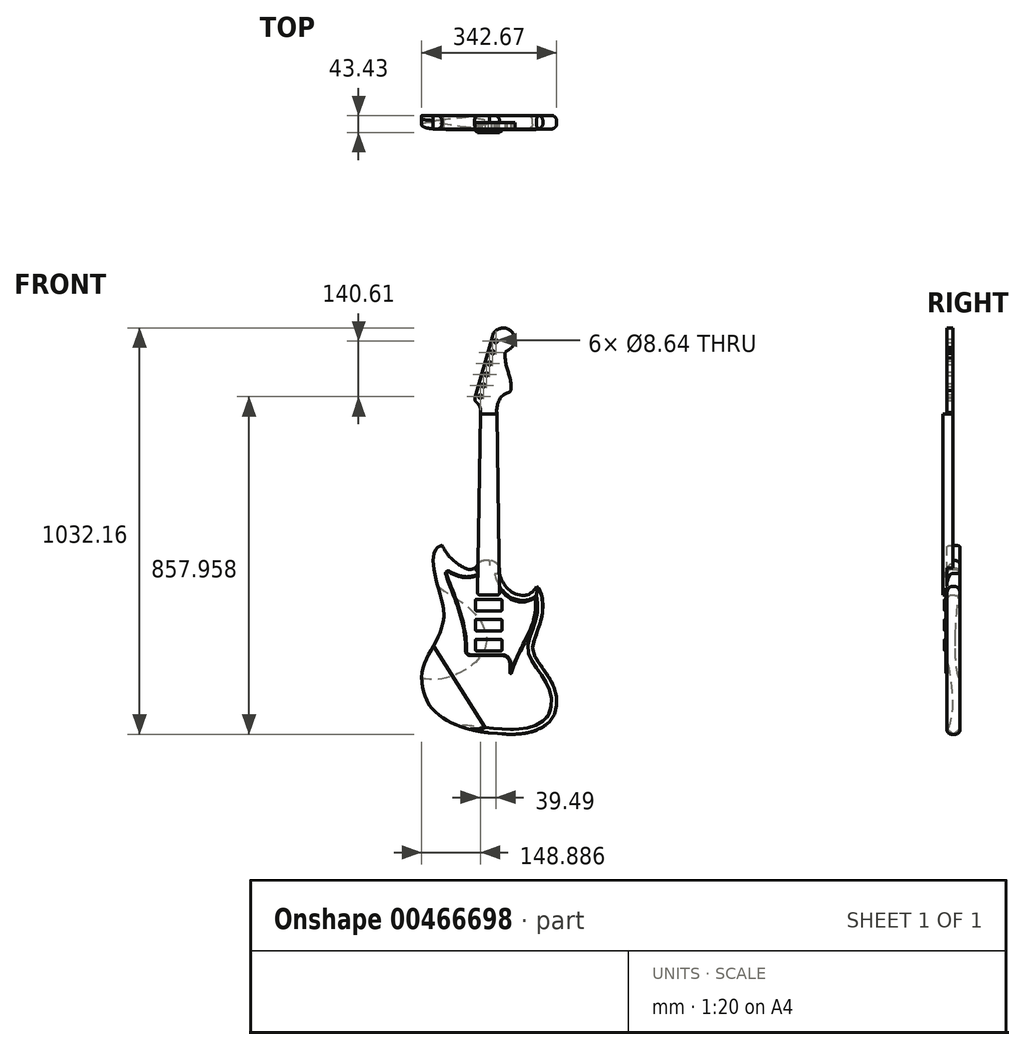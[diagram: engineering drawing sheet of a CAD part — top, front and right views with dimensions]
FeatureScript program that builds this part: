
annotation { "Feature Type Name" : "Feature", "Feature Type Description" : "" }
export const myFeature = defineFeature(function(context is Context, id is Id, definition is map)
    precondition{}
    {
        {
            var Q0;
            Q0=qCreatedBy(makeId("Front.planeOp"),FACE);
            var sketch = newSketch(context, id + "F0", { "sketchPlane" : qUnion([Q0])});
            skPoint(sketch, "E0", {"position": v(266.02, -333.89) * mm});
            skPoint(sketch, "E1", {"position": v(-78.2, -278.93) * mm});
            skPoint(sketch, "E2", {"position": v(-76.64, -280.74) * mm});
            skLineSegment(sketch, "E3", {"start": v(93.45, -416.82) * mm, "end": v(93.45, 154.69) * mm});
            skFitSpline(sketch, "E4", {"points": [v(215.27, -45.07) * mm, v(221.74, -52.76) * mm, v(227.37, -65.34) * mm, v(230.94, -92.4) * mm, v(229.66, -113.64) * mm, v(222.38, -144) * mm, v(207.76, -185.79) * mm, v(205.78, -193.7) * mm, v(205.08, -202.3) * mm, v(212.22, -224.83) * mm, v(254.9, -291.04) * mm, v(266.02, -335.63) * mm, v(264.26, -354.59) * mm, v(260.65, -368.75) * mm, v(250.4, -387.43) * mm, v(215.65, -410.17) * mm, v(172.98, -419.58) * mm, v(137.57, -420.38) * mm, v(93.45, -416.82) * mm], "startDerivative": vector(356.2, -351.19) * mm, "endDerivative": vector(-585.1, 56.64) * mm});
            skFitSpline(sketch, "E5", {"points": [v(121.13, -12.3) * mm, v(148.78, -56.88) * mm, v(178.2, -67.58) * mm, v(196.49, -64.46) * mm, v(215.27, -45.07) * mm], "startDerivative": vector(17.29, -126.3) * mm, "endDerivative": vector(64.81, 113.25) * mm});
            skFitSpline(sketch, "E6", {"points": [v(93.45, -416.82) * mm, v(3.9, -393.73) * mm, v(-39.72, -365.76) * mm, v(-64.89, -332.1) * mm, v(-76.64, -276.03) * mm, v(-67.62, -235.7) * mm, v(-46.7, -196.3) * mm, v(-31.36, -164.8) * mm, v(-22.38, -135.72) * mm, v(-20.36, -121.45) * mm, v(-21.2, -101.5) * mm, v(-32.33, -55.57) * mm, v(-41.85, -21.6) * mm, v(-47.21, 13.16) * mm, v(-45.84, 34.12) * mm, v(-39.8, 50.28) * mm, v(-29.72, 57.62) * mm, v(-25.03, 58.87) * mm], "startDerivative": vector(-990.97, 98.44) * mm, "endDerivative": vector(154.03, 27.77) * mm});
            skFitSpline(sketch, "E7", {"points": [v(-25.03, 58.87) * mm, v(5.76, 19.2) * mm, v(66.93, -2.65) * mm], "startDerivative": vector(61.81, -109.24) * mm, "endDerivative": vector(117.84, 33.66) * mm});
            skArc(sketch, "E8.filletArc", {"start": v(39.05, -0.76) * mm, "mid": v(48.72, -1.75) * mm, "end": v(57.8, 1.72) * mm});
            skLineSegment(sketch, "E9.bottom", {"start": v(95.73, 20.73) * mm, "end": v(95.73, 20.73) * mm});
            skLineSegment(sketch, "E9.top", {"start": v(67.02, -59.63) * mm, "end": v(121.13, -59.63) * mm});
            skLineSegment(sketch, "E9.left", {"start": v(67.02, 11.98) * mm, "end": v(67.02, -59.63) * mm});
            skLineSegment(sketch, "E9.right", {"start": v(121.13, -4.67) * mm, "end": v(121.13, -59.63) * mm});
            skLineSegment(sketch, "E10", {"start": v(93.45, -416.82) * mm, "end": v(-46.7, -196.3) * mm});
            skLineSegment(sketch, "E11.bottom", {"start": v(57.58, -125.48) * mm, "end": v(129.33, -125.48) * mm});
            skLineSegment(sketch, "E11.top", {"start": v(57.58, -161.04) * mm, "end": v(129.33, -161.04) * mm});
            skLineSegment(sketch, "E11.left", {"start": v(49.96, -133.1) * mm, "end": v(49.96, -153.42) * mm});
            skLineSegment(sketch, "E11.right", {"start": v(136.95, -133.1) * mm, "end": v(136.95, -153.42) * mm});
            skArc(sketch, "E12.filletArc", {"start": v(57.58, -125.48) * mm, "mid": v(52.19, -127.7) * mm, "end": v(49.96, -133.1) * mm});
            skArc(sketch, "E13.filletArc", {"start": v(136.95, -133.1) * mm, "mid": v(134.72, -127.7) * mm, "end": v(129.33, -125.48) * mm});
            skArc(sketch, "E14.filletArc", {"start": v(129.33, -161.04) * mm, "mid": v(134.72, -158.8) * mm, "end": v(136.95, -153.42) * mm});
            skArc(sketch, "E15.filletArc", {"start": v(49.96, -153.42) * mm, "mid": v(52.19, -158.8) * mm, "end": v(57.58, -161.04) * mm});
            skLineSegment(sketch, "E16", {"start": v(93.45, -125.48) * mm, "end": v(93.45, -161.04) * mm, "construction": true});
            skLineSegment(sketch, "E17", {"start": v(49.96, -143.26) * mm, "end": v(136.95, -143.26) * mm, "construction": true});
            skLineSegment(sketch, "E18.bottom", {"start": v(57.58, -74.68) * mm, "end": v(129.33, -74.68) * mm});
            skLineSegment(sketch, "E18.top", {"start": v(57.58, -110.24) * mm, "end": v(129.33, -110.24) * mm});
            skLineSegment(sketch, "E18.left", {"start": v(49.96, -82.3) * mm, "end": v(49.96, -102.62) * mm});
            skLineSegment(sketch, "E18.right", {"start": v(136.95, -82.3) * mm, "end": v(136.95, -102.62) * mm});
            skArc(sketch, "E19.filletArc", {"start": v(57.58, -74.68) * mm, "mid": v(52.19, -76.9) * mm, "end": v(49.96, -82.3) * mm});
            skArc(sketch, "E20.filletArc", {"start": v(136.95, -82.3) * mm, "mid": v(134.72, -76.9) * mm, "end": v(129.33, -74.68) * mm});
            skArc(sketch, "E21.filletArc", {"start": v(129.33, -110.24) * mm, "mid": v(134.72, -108) * mm, "end": v(136.95, -102.62) * mm});
            skArc(sketch, "E22.filletArc", {"start": v(49.96, -102.62) * mm, "mid": v(52.19, -108) * mm, "end": v(57.58, -110.24) * mm});
            skLineSegment(sketch, "E23", {"start": v(93.45, -74.68) * mm, "end": v(93.45, -110.24) * mm, "construction": true});
            skLineSegment(sketch, "E24", {"start": v(49.96, -92.46) * mm, "end": v(136.95, -92.46) * mm, "construction": true});
            skLineSegment(sketch, "E25.bottom", {"start": v(57.58, -176.28) * mm, "end": v(129.33, -176.28) * mm});
            skLineSegment(sketch, "E25.top", {"start": v(57.58, -211.84) * mm, "end": v(129.33, -211.84) * mm});
            skLineSegment(sketch, "E25.left", {"start": v(49.96, -183.9) * mm, "end": v(49.96, -204.22) * mm});
            skLineSegment(sketch, "E25.right", {"start": v(136.95, -183.9) * mm, "end": v(136.95, -204.22) * mm});
            skArc(sketch, "E26.filletArc", {"start": v(57.58, -176.28) * mm, "mid": v(52.19, -178.5) * mm, "end": v(49.96, -183.9) * mm});
            skArc(sketch, "E27.filletArc", {"start": v(136.95, -183.9) * mm, "mid": v(134.72, -178.5) * mm, "end": v(129.33, -176.28) * mm});
            skArc(sketch, "E28.filletArc", {"start": v(129.33, -211.84) * mm, "mid": v(134.72, -209.6) * mm, "end": v(136.95, -204.22) * mm});
            skArc(sketch, "E29.filletArc", {"start": v(49.96, -204.22) * mm, "mid": v(52.19, -209.6) * mm, "end": v(57.58, -211.84) * mm});
            skLineSegment(sketch, "E30", {"start": v(93.45, -176.28) * mm, "end": v(93.45, -211.84) * mm, "construction": true});
            skLineSegment(sketch, "E31", {"start": v(49.96, -194.06) * mm, "end": v(136.95, -194.06) * mm, "construction": true});
            skPoint(sketch, "E32.visualSharp", {"position": v(121.13, 20.73) * mm});
            skArc(sketch, "E32.filletArc", {"start": v(121.13, -4.67) * mm, "mid": v(113.7, 13.3) * mm, "end": v(95.73, 20.73) * mm});
            skFitSpline(sketch, "E33", {"points": [v(95.73, 20.73) * mm, v(73.37, 17.96) * mm, v(57.8, 1.72) * mm], "startDerivative": vector(-43.43, -1.27) * mm, "endDerivative": vector(-37.77, -27.72) * mm});
            skSolve(sketch);
        }
        {
            var Q0;
            {var subQ0=sQuery(id+"F0.wireOp",EDGE,"E10");Q0=makeQuery(id+"F0.imprint","IMPRINT",FACE,{"disambiguationData":[TD([[makeQuery(id+"F0.imprint","IMPRINT",EDGE,{"derivedFrom":subQ0}),1.0]])]});}
            extrude(context, id + "F1", {"entities" : qUnion([Q0]), "depth" : 33.9 * mm});
        }
        {
            var Q0;
            Q0=makeQuery(id+"F1.opExtrude","SWEPT_EDGE",EDGE,{"disambiguationData":[OSD([sQuery(id+"F0.wireOp",EDGE,"E3"),sQuery(id+"F0.wireOp",EDGE,"E4"),sQuery(id+"F0.wireOp",EDGE,"E6"),sQuery(id+"F0.wireOp",EDGE,"E10")])]});
            var Q1;
            Q1=sQuery(id+"F0.wireOp",EDGE,"E10");
            cPlane(context, id + "F2", {"entities" : qUnion([Q0, Q1]), "cplaneType" : CPlaneType.LINE_ANGLE, "offset" : 25.4 * mm, "angle" : 90 * degree, "width" : 152.4 * mm, "height" : 152.4 * mm});
        }
        {
            var Q0;
            Q0=qCreatedBy(id+"F2.planeOp",FACE);
            var sketch = newSketch(context, id + "F3", { "sketchPlane" : qUnion([Q0])});
            skFitSpline(sketch, "E34", {"points": [v(-144.71, 33.92) * mm, v(-234.18, 18.01) * mm], "startDerivative": vector(-88.6, -4.87) * mm, "endDerivative": vector(-122.95, -37.49) * mm});
            skLineSegment(sketch, "E35", {"start": v(-234.18, 18.01) * mm, "end": v(-234.18, 35.25) * mm});
            skLineSegment(sketch, "E36", {"start": v(-234.18, 35.25) * mm, "end": v(-144.71, 35.25) * mm});
            skLineSegment(sketch, "E37", {"start": v(-144.71, 33.92) * mm, "end": v(-144.71, 35.25) * mm});
            skSolve(sketch);
        }
        {
            var Q0;
            Q0=makeQuery(id+"F3.imprint","IMPRINT",FACE,{"disambiguationData":[TD([[makeQuery(id+"F3.imprint","IMPRINT",EDGE,{"derivedFrom":sQuery(id+"F3.wireOp",EDGE,"E34")}),-1.0]])]});
            extrude(context, id + "F4", {"entities" : qUnion([Q0]), "operationType" : NewBodyOperationType.REMOVE, "endBound" : BoundingType.THROUGH_ALL, "oppositeDirection" : true, "depth" : 274.32 * mm});
        }
        {
            var Q0;
            {var subQ1=sQuery(id+"F0.wireOp",EDGE,"E7");Q0=makeQuery(id+"F0.imprint","IMPRINT",FACE,{"disambiguationData":[TD([[makeQuery(id+"F0.imprint","IMPRINT",EDGE,{"derivedFrom":subQ1}),-1.0]])]});}
            var Q1;
            {var subQ5=sQuery(id+"F0.wireOp",EDGE,"E4");Q1=makeQuery(id+"F0.imprint","IMPRINT",FACE,{"disambiguationData":[TD([[makeQuery(id+"F0.imprint","IMPRINT",EDGE,{"derivedFrom":subQ5}),-1.0]])]});}
            var Q2;
            {var subQ2=sQuery(id+"F0.wireOp",EDGE,"E9.bottom");var subQ4=sQuery(id+"F0.wireOp",EDGE,"E3");var subQ5=makeQuery(id+"F0.imprint","INTERSECT",VERTEX,{"derivedFrom":[subQ4,subQ2]});Q2=makeQuery(id+"F0.imprint","IMPRINT",FACE,{"disambiguationData":[TD([[makeQuery(id+"F0.imprint","IMPRINT",EDGE,{"disambiguationData":[TD([[subQ5,1.0]])],"derivedFrom":subQ4}),-1.0]])]});}
            var Q3;
            {var subQ2=sQuery(id+"F0.wireOp",EDGE,"E9.bottom");var subQ4=sQuery(id+"F0.wireOp",EDGE,"E3");var subQ5=makeQuery(id+"F0.imprint","INTERSECT",VERTEX,{"derivedFrom":[subQ4,subQ2]});Q3=makeQuery(id+"F0.imprint","IMPRINT",FACE,{"disambiguationData":[TD([[makeQuery(id+"F0.imprint","IMPRINT",EDGE,{"disambiguationData":[TD([[subQ5,1.0]])],"derivedFrom":subQ4}),1.0]])]});}
            var Q4;
            Q4=makeQuery(id+"F0.imprint","IMPRINT",FACE,{"disambiguationData":[TD([[makeQuery(id+"F0.imprint","IMPRINT",EDGE,{"derivedFrom":sQuery(id+"F0.wireOp",EDGE,"E18.right")}),-1.0]])]});
            var Q5;
            Q5=makeQuery(id+"F0.imprint","IMPRINT",FACE,{"disambiguationData":[TD([[makeQuery(id+"F0.imprint","IMPRINT",EDGE,{"derivedFrom":sQuery(id+"F0.wireOp",EDGE,"E18.left")}),1.0]])]});
            var Q6;
            Q6=makeQuery(id+"F0.imprint","IMPRINT",FACE,{"disambiguationData":[TD([[makeQuery(id+"F0.imprint","IMPRINT",EDGE,{"derivedFrom":sQuery(id+"F0.wireOp",EDGE,"E11.left")}),1.0]])]});
            var Q7;
            Q7=makeQuery(id+"F0.imprint","IMPRINT",FACE,{"disambiguationData":[TD([[makeQuery(id+"F0.imprint","IMPRINT",EDGE,{"derivedFrom":sQuery(id+"F0.wireOp",EDGE,"E11.right")}),-1.0]])]});
            var Q8;
            Q8=makeQuery(id+"F0.imprint","IMPRINT",FACE,{"disambiguationData":[TD([[makeQuery(id+"F0.imprint","IMPRINT",EDGE,{"derivedFrom":sQuery(id+"F0.wireOp",EDGE,"E25.right")}),-1.0]])]});
            var Q9;
            Q9=makeQuery(id+"F0.imprint","IMPRINT",FACE,{"disambiguationData":[TD([[makeQuery(id+"F0.imprint","IMPRINT",EDGE,{"derivedFrom":sQuery(id+"F0.wireOp",EDGE,"E25.left")}),1.0]])]});
            var Q10;
            {var subQ8=sQuery(id+"F0.wireOp",EDGE,"E32.filletArc");Q10=makeQuery(id+"F0.imprint","IMPRINT",FACE,{"disambiguationData":[TD([[makeQuery(id+"F0.imprint","IMPRINT",EDGE,{"derivedFrom":subQ8}),1.0]])]});}
            var Q11;
            {var subQ5=sQuery(id+"F0.wireOp",EDGE,"E9.left");Q11=makeQuery(id+"F0.imprint","IMPRINT",FACE,{"disambiguationData":[TD([[makeQuery(id+"F0.imprint","IMPRINT",EDGE,{"derivedFrom":subQ5}),1.0]])]});}
            extrude(context, id + "F5", {"entities" : qUnion([Q0, Q1, Q2, Q3, Q4, Q5, Q6, Q7, Q8, Q9, Q10, Q11]), "operationType" : NewBodyOperationType.ADD, "depth" : 33.9 * mm});
        }
        {
            var Q0;
            {var subQ1=sQuery(id+"F0.wireOp",EDGE,"E7");Q0=makeQuery(id+"F0.imprint","IMPRINT",FACE,{"disambiguationData":[TD([[makeQuery(id+"F0.imprint","IMPRINT",EDGE,{"derivedFrom":subQ1}),-1.0]])]});}
            var sketch = newSketch(context, id + "F6", { "sketchPlane" : qUnion([Q0])});
            skFitSpline(sketch, "E38", {"points": [v(-56.72, -25.02) * mm, v(27.3, -87.2) * mm, v(83.7, -155.44) * mm, v(73.57, -221.77) * mm, v(-76.43, -278.56) * mm], "startDerivative": vector(46.73, -161.4) * mm, "endDerivative": vector(-591.69, 127.24) * mm});
            skLineSegment(sketch, "E39", {"start": v(-56.72, -25.02) * mm, "end": v(-76.43, -278.56) * mm});
            skLineSegment(sketch, "E40", {"start": v(87.74, -184.34) * mm, "end": v(-206.93, -143.72) * mm});
            skSolve(sketch);
        }
        {
            var Q0;
            Q0=sQuery(id+"F6.wireOp",EDGE,"E40");
            cPlane(context, id + "F7", {"entities" : qUnion([Q0]), "cplaneType" : CPlaneType.LINE_ANGLE, "offset" : 25.4 * mm, "angle" : 90 * degree, "width" : 152.4 * mm, "height" : 152.4 * mm});
        }
        {
            var Q0;
            Q0=qCreatedBy(id+"F7.planeOp",FACE);
            var sketch = newSketch(context, id + "F8", { "sketchPlane" : qUnion([Q0])});
            skLineSegment(sketch, "E41", {"start": v(112.3, 0) * mm, "end": v(-53.56, -16.1) * mm});
            skSolve(sketch);
        }
        {
            var Q0;
            {var subQ0=sQuery(id+"F6.wireOp",EDGE,"E40");var subQ1=sQuery(id+"F6.wireOp",EDGE,"E38");var subQ2=makeQuery(id+"F6.imprint","INTERSECT",VERTEX,{"derivedFrom":[subQ1,subQ0]});Q0=makeQuery(id+"F6.imprint","IMPRINT",FACE,{"disambiguationData":[TD([[makeQuery(id+"F6.imprint","IMPRINT",EDGE,{"disambiguationData":[TD([[subQ2,1.0]])],"derivedFrom":subQ1}),-1.0]])]});}
            var Q1;
            {var subQ0=sQuery(id+"F6.wireOp",EDGE,"E40");var subQ1=sQuery(id+"F6.wireOp",EDGE,"E38");var subQ2=makeQuery(id+"F6.imprint","INTERSECT",VERTEX,{"derivedFrom":[subQ1,subQ0]});Q1=makeQuery(id+"F6.imprint","IMPRINT",FACE,{"disambiguationData":[TD([[makeQuery(id+"F6.imprint","IMPRINT",EDGE,{"disambiguationData":[TD([[subQ2,-1.0]])],"derivedFrom":subQ1}),-1.0]])]});}
            var Q2;
            {var subQ7=sQuery(id+"F6.wireOp",EDGE,"E39");var subQ8=sQuery(id+"F6.wireOp",EDGE,"E38");var subQ9=makeQuery(id+"F6.imprint","INTERSECT",VERTEX,{"disambiguationData":[OD(1.0)],"derivedFrom":[subQ8,subQ7]});Q2=makeQuery(id+"F6.imprint","IMPRINT",FACE,{"disambiguationData":[TD([[makeQuery(id+"F6.imprint","IMPRINT",EDGE,{"disambiguationData":[TD([[subQ9,1.0]])],"derivedFrom":subQ8}),-1.0]])]});}
            var Q3;
            {var subQ0=sQuery(id+"F6.wireOp",EDGE,"E39");var subQ1=sQuery(id+"F6.wireOp",EDGE,"E38");var subQ2=makeQuery(id+"F6.imprint","INTERSECT",VERTEX,{"disambiguationData":[OD(0.0)],"derivedFrom":[subQ1,subQ0]});Q3=makeQuery(id+"F6.imprint","IMPRINT",FACE,{"disambiguationData":[TD([[makeQuery(id+"F6.imprint","IMPRINT",EDGE,{"disambiguationData":[TD([[subQ2,-1.0]])],"derivedFrom":subQ0}),1.0]])]});}
            var Q4;
            {var subQ9=sQuery(id+"F0.wireOp",EDGE,"E29.filletArc");var subQ10=makeQuery(id+"F0.imprint","IMPRINT",EDGE,{"derivedFrom":subQ9});Q4=makeQuery(id+"F6.imprint","IMPRINT",FACE,{"disambiguationData":[TD([[makeQuery(id+"F6.imprint","IMPRINT",EDGE,{"derivedFrom":subQ10}),-1.0]])]});}
            var Q5;
            Q5=makeQuery(id+"F6.imprint","IMPRINT",FACE,{"disambiguationData":[TD([[makeQuery(id+"F6.imprint","IMPRINT",EDGE,{"derivedFrom":makeQuery(id+"F0.imprint","IMPRINT",EDGE,{"derivedFrom":sQuery(id+"F0.wireOp",EDGE,"E11.left")})}),-1.0]])]});
            var Q6;
            Q6=makeQuery(id+"F6.imprint","IMPRINT",FACE,{"disambiguationData":[TD([[makeQuery(id+"F6.imprint","IMPRINT",EDGE,{"derivedFrom":makeQuery(id+"F0.imprint","IMPRINT",EDGE,{"derivedFrom":sQuery(id+"F0.wireOp",EDGE,"E11.left")})}),1.0]])]});
            var Q7;
            Q7=sQuery(id+"F8.wireOp",EDGE,"E41");
            sweep(context, id + "F9", {"operationType" : NewBodyOperationType.REMOVE, "profiles" : qUnion([Q0, Q1, Q2, Q3, Q4, Q5, Q6]), "path" : qUnion([Q7])});
        }
        {
            var Q0;
            {var subQ0=sQuery(id+"F0.wireOp",EDGE,"E10");var subQ1=sQuery(id+"F0.wireOp",EDGE,"E6");Q0=makeQuery(id+"F5.boolean.opBoolean","MERGE",FACE,{"derivedFrom":[makeQuery(id+"F1.opExtrude","CAP_FACE",FACE,{"disambiguationData":[OSD([subQ1,subQ0])],"isStart":false}),makeQuery(id+"F5.opExtrude","CAP_FACE",FACE,{"disambiguationData":[OSD([sQuery(id+"F0.wireOp",EDGE,"E4"),sQuery(id+"F0.wireOp",EDGE,"E5"),subQ1,sQuery(id+"F0.wireOp",EDGE,"E7"),sQuery(id+"F0.wireOp",EDGE,"E8.filletArc"),sQuery(id+"F0.wireOp",EDGE,"E9.bottom"),sQuery(id+"F0.wireOp",EDGE,"E9.right"),subQ0,sQuery(id+"F0.wireOp",EDGE,"E11.bottom"),sQuery(id+"F0.wireOp",EDGE,"E11.top"),sQuery(id+"F0.wireOp",EDGE,"E11.left"),sQuery(id+"F0.wireOp",EDGE,"E11.right"),sQuery(id+"F0.wireOp",EDGE,"E12.filletArc"),sQuery(id+"F0.wireOp",EDGE,"E13.filletArc"),sQuery(id+"F0.wireOp",EDGE,"E14.filletArc"),sQuery(id+"F0.wireOp",EDGE,"E15.filletArc"),sQuery(id+"F0.wireOp",EDGE,"E18.bottom"),sQuery(id+"F0.wireOp",EDGE,"E18.top"),sQuery(id+"F0.wireOp",EDGE,"E18.left"),sQuery(id+"F0.wireOp",EDGE,"E18.right"),sQuery(id+"F0.wireOp",EDGE,"E19.filletArc"),sQuery(id+"F0.wireOp",EDGE,"E20.filletArc"),sQuery(id+"F0.wireOp",EDGE,"E21.filletArc"),sQuery(id+"F0.wireOp",EDGE,"E22.filletArc"),sQuery(id+"F0.wireOp",EDGE,"E25.bottom"),sQuery(id+"F0.wireOp",EDGE,"E25.top"),sQuery(id+"F0.wireOp",EDGE,"E25.left"),sQuery(id+"F0.wireOp",EDGE,"E25.right"),sQuery(id+"F0.wireOp",EDGE,"E26.filletArc"),sQuery(id+"F0.wireOp",EDGE,"E27.filletArc"),sQuery(id+"F0.wireOp",EDGE,"E28.filletArc"),sQuery(id+"F0.wireOp",EDGE,"E29.filletArc"),sQuery(id+"F0.wireOp",EDGE,"E32.filletArc"),sQuery(id+"F0.wireOp",EDGE,"5da029f0-0d08-4df7-a96a-8b1ca544c31f.filletArc")])],"isStart":false})]});}
            var sketch = newSketch(context, id + "F10", { "sketchPlane" : qUnion([Q0])});
            skLineSegment(sketch, "E42", {"start": v(114.09, 393.44) * mm, "end": v(72.81, 393.44) * mm});
            skArc(sketch, "E43", {"start": v(152.05, 562.26) * mm, "mid": v(145.08, 607.74) * mm, "end": v(102.61, 590.03) * mm});
            skLineSegment(sketch, "E44", {"start": v(114.09, 396.48) * mm, "end": v(72.81, 396.48) * mm});
            skArc(sketch, "E45", {"start": v(139.6, 553.2) * mm, "mid": v(136.44, 550.5) * mm, "end": v(134.97, 546.6) * mm});
            skFitSpline(sketch, "E46", {"points": [v(134.97, 546.6) * mm, v(134.92, 539.54) * mm, v(135.3, 534.72) * mm], "startDerivative": vector(-2.42, -13.24) * mm, "endDerivative": vector(1.68, -15.84) * mm});
            skFitSpline(sketch, "E47", {"points": [v(135.3, 534.72) * mm, v(136.98, 522.82) * mm, v(141.32, 505.32) * mm, v(145.61, 491.19) * mm, v(149.98, 471.63) * mm, v(150.16, 455.36) * mm, v(149.34, 452.34) * mm], "startDerivative": vector(10.58, -89.44) * mm, "endDerivative": vector(-11.19, -29.44) * mm});
            skFitSpline(sketch, "E48", {"points": [v(152.05, 562.26) * mm, v(147, 557.6) * mm, v(141.78, 554.47) * mm, v(139.6, 553.2) * mm], "startDerivative": vector(-11.63, -12.96) * mm, "endDerivative": vector(-8.03, -4.83) * mm});
            skLineSegment(sketch, "E49", {"start": v(102.61, 590.03) * mm, "end": v(59.05, 434.9) * mm});
            skFitSpline(sketch, "E50", {"points": [v(114.09, 396.48) * mm, v(114.26, 407.46) * mm, v(116.53, 419.52) * mm, v(118.87, 425.81) * mm, v(123.45, 433.9) * mm, v(131.73, 441.98) * mm, v(139.43, 446.23) * mm, v(146.53, 449.2) * mm, v(148.1, 450.53) * mm, v(149.34, 452.34) * mm], "startDerivative": vector(-2.24, 78.28) * mm, "endDerivative": vector(20.59, 31.93) * mm});
            skFitSpline(sketch, "E51", {"points": [v(72.81, 396.48) * mm, v(72.81, 400.36) * mm, v(72.71, 404.86) * mm, v(71.11, 411.28) * mm, v(68.48, 416.27) * mm, v(63.92, 421.76) * mm, v(60.07, 425.65) * mm], "startDerivative": vector(-0.26, 27.66) * mm, "endDerivative": vector(-26.41, 27.38) * mm});
            skFitSpline(sketch, "E52", {"points": [v(60.07, 425.65) * mm, v(59.17, 426.96) * mm, v(58.58, 428.1) * mm, v(58.35, 429.15) * mm, v(58.4, 430.68) * mm, v(58.53, 431.89) * mm, v(58.76, 433.48) * mm, v(59.05, 434.9) * mm], "startDerivative": vector(-9.65, 12.38) * mm, "endDerivative": vector(1.99, 9.31) * mm});
            skLineSegment(sketch, "E53", {"start": v(114.09, 396.48) * mm, "end": v(114.09, 393.44) * mm});
            skLineSegment(sketch, "E54", {"start": v(72.81, 396.48) * mm, "end": v(72.81, 393.44) * mm});
            skLineSegment(sketch, "E55", {"start": v(93.45, 393.44) * mm, "end": v(93.45, -76) * mm, "construction": true});
            skLineSegment(sketch, "E56", {"start": v(93.45, -56.52) * mm, "end": v(65.66, -56.52) * mm});
            skLineSegment(sketch, "E57", {"start": v(93.45, -56.52) * mm, "end": v(121.24, -56.52) * mm});
            skLineSegment(sketch, "E58", {"start": v(121.24, -56.52) * mm, "end": v(114.09, 393.44) * mm});
            skLineSegment(sketch, "E59", {"start": v(72.81, 393.44) * mm, "end": v(65.66, -56.52) * mm});
            skLineSegment(sketch, "E60", {"start": v(114.96, -67.31) * mm, "end": v(71.94, -67.31) * mm});
            skLineSegment(sketch, "E61", {"start": v(121.24, -56.52) * mm, "end": v(121.3, -60.86) * mm});
            skLineSegment(sketch, "E62", {"start": v(65.66, -56.52) * mm, "end": v(65.6, -60.86) * mm});
            skArc(sketch, "E63", {"start": v(65.6, -60.86) * mm, "mid": v(67.42, -65.42) * mm, "end": v(71.94, -67.31) * mm});
            skArc(sketch, "E64", {"start": v(114.96, -67.31) * mm, "mid": v(119.48, -65.42) * mm, "end": v(121.3, -60.86) * mm});
            skLineSegment(sketch, "E65", {"start": v(64.88, 411.04) * mm, "end": v(127, 632.25) * mm});
            skCircle(sketch, "E66", {"center": v(111.74, 577.89) * mm, "radius": 4.32 * mm});
            skCircle(sketch, "E67", {"center": v(103.84, 549.77) * mm, "radius": 4.32 * mm});
            skCircle(sketch, "E68", {"center": v(95.94, 521.64) * mm, "radius": 4.32 * mm});
            skCircle(sketch, "E69", {"center": v(88.04, 493.52) * mm, "radius": 4.32 * mm});
            skCircle(sketch, "E70", {"center": v(80.14, 465.4) * mm, "radius": 4.32 * mm});
            skCircle(sketch, "E71", {"center": v(72.25, 437.28) * mm, "radius": 4.32 * mm});
            skLineSegment(sketch, "E72", {"start": v(93.45, 370.83) * mm, "end": v(93.45, -10.17) * mm});
            skPoint(sketch, "E73", {"position": v(93.4, -232.04) * mm});
            skPoint(sketch, "E73.positionSnap0", {"position": v(93.4, -211.03) * mm});
            skSolve(sketch);
        }
        {
            var Q0;
            {var subQ9=sQuery(id+"F10.wireOp",EDGE,"E56");Q0=makeQuery(id+"F10.imprint","IMPRINT",FACE,{"disambiguationData":[TD([[makeQuery(id+"F10.imprint","IMPRINT",EDGE,{"derivedFrom":subQ9}),1.0]])]});}
            var Q1;
            {var subQ0=sQuery(id+"F10.wireOp",EDGE,"E61");Q1=makeQuery(id+"F10.imprint","IMPRINT",FACE,{"disambiguationData":[TD([[makeQuery(id+"F10.imprint","IMPRINT",EDGE,{"derivedFrom":subQ0}),-1.0]])]});}
            var Q2;
            {var subQ1=sQuery(id+"F10.wireOp",EDGE,"E42");Q2=makeQuery(id+"F10.imprint","IMPRINT",FACE,{"disambiguationData":[TD([[makeQuery(id+"F10.imprint","IMPRINT",EDGE,{"derivedFrom":subQ1}),1.0]])]});}
            var Q3;
            {var subQ1=sQuery(id+"F10.wireOp",EDGE,"E56");Q3=makeQuery(id+"F10.imprint","IMPRINT",FACE,{"disambiguationData":[TD([[makeQuery(id+"F10.imprint","IMPRINT",EDGE,{"derivedFrom":subQ1}),-1.0]])]});}
            var Q4;
            {var subQ1=sQuery(id+"F10.wireOp",EDGE,"E44");Q4=makeQuery(id+"F10.imprint","IMPRINT",FACE,{"disambiguationData":[TD([[makeQuery(id+"F10.imprint","IMPRINT",EDGE,{"derivedFrom":subQ1}),-1.0]])]});}
            var Q5;
            {var subQ9=sQuery(id+"F10.wireOp",EDGE,"E49");Q5=makeQuery(id+"F10.imprint","IMPRINT",FACE,{"disambiguationData":[TD([[makeQuery(id+"F10.imprint","IMPRINT",EDGE,{"derivedFrom":subQ9}),1.0]])]});}
            var Q6;
            Q6=makeQuery(id+"F10.imprint","IMPRINT",FACE,{"disambiguationData":[TD([[makeQuery(id+"F10.imprint","IMPRINT",EDGE,{"derivedFrom":sQuery(id+"F10.wireOp",EDGE,"E42")}),-1.0]])]});
            var Q7;
            Q7 = qSketchRegion(id + "F8", true);
            extrude(context, id + "F11", {"entities" : qUnion([Q0, Q1, Q2, Q3, Q4, Q5, Q6, Q7]), "operationType" : NewBodyOperationType.ADD, "oppositeDirection" : true, "depth" : 15.88 * mm});
        }
        {
            var Q0;
            {var subQ9=sQuery(id+"F10.wireOp",EDGE,"E56");Q0=makeQuery(id+"F10.imprint","IMPRINT",FACE,{"disambiguationData":[TD([[makeQuery(id+"F10.imprint","IMPRINT",EDGE,{"derivedFrom":subQ9}),1.0]])]});}
            var Q1;
            {var subQ0=sQuery(id+"F10.wireOp",EDGE,"E61");Q1=makeQuery(id+"F10.imprint","IMPRINT",FACE,{"disambiguationData":[TD([[makeQuery(id+"F10.imprint","IMPRINT",EDGE,{"derivedFrom":subQ0}),-1.0]])]});}
            var Q2;
            {var subQ1=sQuery(id+"F10.wireOp",EDGE,"E42");Q2=makeQuery(id+"F10.imprint","IMPRINT",FACE,{"disambiguationData":[TD([[makeQuery(id+"F10.imprint","IMPRINT",EDGE,{"derivedFrom":subQ1}),1.0]])]});}
            var Q3;
            {var subQ1=sQuery(id+"F10.wireOp",EDGE,"E56");Q3=makeQuery(id+"F10.imprint","IMPRINT",FACE,{"disambiguationData":[TD([[makeQuery(id+"F10.imprint","IMPRINT",EDGE,{"derivedFrom":subQ1}),-1.0]])]});}
            extrude(context, id + "F12", {"entities" : qUnion([Q0, Q1, Q2, Q3]), "operationType" : NewBodyOperationType.ADD, "depth" : 9.52 * mm});
        }
        {
            var Q0;
            {var subQ0=sQuery(id+"F0.wireOp",EDGE,"E6");Q0=makeQuery(id+"F5.boolean.opBoolean","MERGE",EDGE,{"derivedFrom":[makeQuery(id+"F4.boolean.opBoolean","SPLIT",EDGE,{"disambiguationData":[OD(1.0)],"derivedFrom":makeQuery(id+"F1.opExtrude","CAP_EDGE",EDGE,{"disambiguationData":[OSD([subQ0])],"isStart":false})}),makeQuery(id+"F5.opExtrude","CAP_EDGE",EDGE,{"disambiguationData":[OSD([subQ0])],"isStart":false})]});}
            var Q1;
            Q1=makeQuery(id+"F5.opExtrude","CAP_EDGE",EDGE,{"disambiguationData":[OSD([sQuery(id+"F0.wireOp",EDGE,"E4")])],"isStart":true});
            var Q2;
            Q2=makeQuery(id+"F5.opExtrude","CAP_EDGE",EDGE,{"disambiguationData":[OSD([sQuery(id+"F0.wireOp",EDGE,"E4")])],"isStart":false});
            var Q3;
            Q3=makeQuery(id+"F5.opExtrude","CAP_EDGE",EDGE,{"disambiguationData":[OSD([sQuery(id+"F0.wireOp",EDGE,"E5")])],"isStart":false});
            var Q4;
            Q4=makeQuery(id+"F5.opExtrude","CAP_EDGE",EDGE,{"disambiguationData":[OSD([sQuery(id+"F0.wireOp",EDGE,"E5")])],"isStart":true});
            var Q5;
            Q5=makeQuery(id+"F5.opExtrude","CAP_EDGE",EDGE,{"disambiguationData":[OSD([sQuery(id+"F0.wireOp",EDGE,"E7")])],"isStart":true});
            var Q6;
            Q6=makeQuery(id+"F5.opExtrude","CAP_EDGE",EDGE,{"disambiguationData":[OSD([sQuery(id+"F0.wireOp",EDGE,"E7")])],"isStart":false});
            var Q7;
            {var subQ1=sQuery(id+"F0.wireOp",EDGE,"E7");var subQ2=sQuery(id+"F0.wireOp",EDGE,"E6");Q7=makeQuery(id+"F9.boolean.opBoolean","SPLIT",EDGE,{"disambiguationData":[TD([makeQuery(id+"F5.opExtrude","SWEPT_FACE",FACE,{"disambiguationData":[OSD([subQ1])]})])],"derivedFrom":makeQuery(id+"F5.boolean.opBoolean","MERGE",EDGE,{"derivedFrom":[makeQuery(id+"F1.opExtrude","CAP_EDGE",EDGE,{"disambiguationData":[OSD([subQ2])],"isStart":true}),makeQuery(id+"F5.opExtrude","CAP_EDGE",EDGE,{"disambiguationData":[OSD([subQ2])],"isStart":true})]})});}
            var Q8;
            Q8=makeQuery(id+"F5.opExtrude","CAP_EDGE",EDGE,{"disambiguationData":[OSD([sQuery(id+"F0.wireOp",EDGE,"E8.filletArc")])],"isStart":true});
            var Q9;
            Q9=makeQuery(id+"F5.opExtrude","CAP_EDGE",EDGE,{"disambiguationData":[OSD([sQuery(id+"F0.wireOp",EDGE,"E33")])],"isStart":true});
            var Q10;
            Q10=makeQuery(id+"F5.opExtrude","CAP_EDGE",EDGE,{"disambiguationData":[OSD([sQuery(id+"F0.wireOp",EDGE,"E32.filletArc")])],"isStart":true});
            var Q11;
            Q11=makeQuery(id+"F5.opExtrude","CAP_EDGE",EDGE,{"disambiguationData":[OSD([sQuery(id+"F0.wireOp",EDGE,"E8.filletArc")])],"isStart":false});
            var Q12;
            Q12=makeQuery(id+"F5.opExtrude","CAP_EDGE",EDGE,{"disambiguationData":[OSD([sQuery(id+"F0.wireOp",EDGE,"E33")])],"isStart":false});
            fillet(context, id + "F13", {"entities" : qUnion([Q0, Q1, Q2, Q3, Q4, Q5, Q6, Q7, Q8, Q9, Q10, Q11, Q12]), "radius" : 12.7 * mm, "tangentPropagation" : true, "allowEdgeOverflow" : false});
        }
        {
            var Q0;
            Q0=makeQuery(id+"F10.imprint","IMPRINT",FACE,{"disambiguationData":[TD([[makeQuery(id+"F10.imprint","IMPRINT",EDGE,{"derivedFrom":sQuery(id+"F10.wireOp",EDGE,"E60")}),1.0]])]});
            var sketch = newSketch(context, id + "F14", { "sketchPlane" : qUnion([Q0])});
            skFitSpline(sketch, "E74.0", {"points": [v(214.49, -66.79) * mm, v(213.66, -67.6) * mm, v(211.95, -69.17) * mm, v(209.26, -71.36) * mm, v(206.42, -73.38) * mm, v(203.48, -75.17) * mm, v(200.43, -76.7) * mm, v(197.78, -77.77) * mm, v(195.6, -78.5) * mm, v(193.92, -78.96) * mm, v(192.22, -79.37) * mm, v(189.96, -79.8) * mm, v(187.1, -80.18) * mm, v(183.67, -80.4) * mm, v(180.22, -80.4) * mm, v(176.76, -80.24) * mm, v(173.3, -79.94) * mm, v(169.86, -79.49) * mm, v(166.48, -78.87) * mm, v(163.14, -78.08) * mm, v(159.86, -77.11) * mm, v(156.62, -75.96) * mm, v(153.97, -74.83) * mm, v(151.88, -73.84) * mm, v(149.82, -72.78) * mm, v(147.33, -71.36) * mm, v(144.44, -69.5) * mm, v(141.67, -67.48) * mm, v(139, -65.32) * mm, v(136.44, -63.01) * mm, v(133.97, -60.58) * mm, v(131.6, -58.07) * mm, v(128.57, -54.6) * mm, v(125.01, -50.1) * mm, v(122.39, -46.3) * mm, v(121.13, -44.37) * mm]});
            skPoint(sketch, "E75", {"position": v(195.9, -173.4) * mm});
            skLineSegment(sketch, "E76.0", {"start": v(114.96, -67.31) * mm, "end": v(71.94, -67.31) * mm});
            skLineSegment(sketch, "E77.0", {"start": v(72.81, 393.44) * mm, "end": v(65.66, -56.52) * mm});
            skArc(sketch, "E77.1", {"start": v(65.6, -60.86) * mm, "mid": v(67.42, -65.42) * mm, "end": v(71.94, -67.31) * mm});
            skLineSegment(sketch, "E77.2", {"start": v(65.66, -56.52) * mm, "end": v(65.6, -60.86) * mm});
            skArc(sketch, "E77.4", {"start": v(114.96, -67.31) * mm, "mid": v(119.48, -65.42) * mm, "end": v(121.3, -60.86) * mm});
            skLineSegment(sketch, "E77.5", {"start": v(121.24, -56.52) * mm, "end": v(121.3, -60.86) * mm});
            skLineSegment(sketch, "E77.6", {"start": v(121.24, -56.52) * mm, "end": v(114.09, 393.44) * mm});
            skLineSegment(sketch, "E78", {"start": v(128.03, -220.8) * mm, "end": v(47.2, -220.8) * mm});
            skFitSpline(sketch, "E79", {"points": [v(-14.28, 18.92) * mm, v(33.57, -220.8) * mm], "startDerivative": vector(-78.7, -56.76) * mm, "endDerivative": vector(-34.73, -324.16) * mm});
            skFitSpline(sketch, "E80", {"points": [v(66.36, -12.5) * mm, v(-19.27, 5.06) * mm], "startDerivative": vector(-83.12, -57.76) * mm, "endDerivative": vector(-38.73, 50.92) * mm});
            skArc(sketch, "E81.filletArc", {"start": v(34.51, -207.63) * mm, "mid": v(38.06, -216.91) * mm, "end": v(47.2, -220.8) * mm});
            skArc(sketch, "E82.filletArc", {"start": v(-6.06, -6.48) * mm, "mid": v(-13.3, -6.73) * mm, "end": v(-15.59, -13.61) * mm});
            skPoint(sketch, "E83.visualSharp", {"position": v(213.22, -71.38) * mm});
            skArc(sketch, "E83.filletArc", {"start": v(214.97, -81.7) * mm, "mid": v(211.52, -76.73) * mm, "end": v(205.47, -76.9) * mm});
            skLineSegment(sketch, "E84", {"start": v(147.08, -239.85) * mm, "end": v(147.08, -263.52) * mm});
            skFitSpline(sketch, "E85", {"points": [v(121.1, -48.9) * mm, v(205.47, -76.9) * mm], "startDerivative": vector(63.8, -99.8) * mm, "endDerivative": vector(87.95, 50.16) * mm});
            skFitSpline(sketch, "E86", {"points": [v(214.97, -81.7) * mm, v(147.08, -290.82) * mm], "startDerivative": vector(14.01, -250.11) * mm, "endDerivative": vector(-25.69, -242.01) * mm});
            skPoint(sketch, "E87.visualSharp", {"position": v(147.08, -220.8) * mm});
            skArc(sketch, "E87.filletArc", {"start": v(147.08, -239.85) * mm, "mid": v(141.5, -226.38) * mm, "end": v(128.03, -220.8) * mm});
            skArc(sketch, "E88.filletArc", {"start": v(147.08, -263.52) * mm, "mid": v(149.29, -266.04) * mm, "end": v(152.07, -264.18) * mm});
            skLineSegment(sketch, "E89.bottom", {"start": v(62.28, -179.39) * mm, "end": v(124.63, -179.39) * mm});
            skLineSegment(sketch, "E89.top", {"start": v(62.28, -208.73) * mm, "end": v(124.63, -208.73) * mm});
            skLineSegment(sketch, "E89.left", {"start": v(59.74, -181.93) * mm, "end": v(59.74, -206.19) * mm});
            skLineSegment(sketch, "E89.right", {"start": v(127.17, -181.93) * mm, "end": v(127.17, -206.19) * mm});
            skLineSegment(sketch, "E90.0", {"start": v(93.45, -416.82) * mm, "end": v(93.45, 154.69) * mm});
            skLineSegment(sketch, "E91", {"start": v(93.45, -208.73) * mm, "end": v(93.45, -179.39) * mm, "construction": true});
            skLineSegment(sketch, "E92", {"start": v(127.17, -194.06) * mm, "end": v(59.74, -194.06) * mm, "construction": true});
            skLineSegment(sketch, "E93.0", {"start": v(49.96, -194.06) * mm, "end": v(136.95, -194.06) * mm, "construction": true});
            skPoint(sketch, "E94.visualSharp", {"position": v(59.74, -208.73) * mm});
            skArc(sketch, "E94.filletArc", {"start": v(59.74, -206.19) * mm, "mid": v(60.48, -207.98) * mm, "end": v(62.28, -208.73) * mm});
            skPoint(sketch, "E95.visualSharp", {"position": v(127.17, -208.73) * mm});
            skArc(sketch, "E95.filletArc", {"start": v(124.63, -208.73) * mm, "mid": v(126.43, -207.98) * mm, "end": v(127.17, -206.19) * mm});
            skPoint(sketch, "E96.visualSharp", {"position": v(127.17, -179.39) * mm});
            skArc(sketch, "E96.filletArc", {"start": v(127.17, -181.93) * mm, "mid": v(126.43, -180.13) * mm, "end": v(124.63, -179.39) * mm});
            skPoint(sketch, "E97.visualSharp", {"position": v(59.74, -179.39) * mm});
            skArc(sketch, "E97.filletArc", {"start": v(62.28, -179.39) * mm, "mid": v(60.48, -180.13) * mm, "end": v(59.74, -181.93) * mm});
            skLineSegment(sketch, "E98.0", {"start": v(49.96, -143.26) * mm, "end": v(136.95, -143.26) * mm, "construction": true});
            skLineSegment(sketch, "E99.0", {"start": v(49.96, -92.46) * mm, "end": v(136.95, -92.46) * mm, "construction": true});
            skLineSegment(sketch, "E100.bottom", {"start": v(62.28, -128.59) * mm, "end": v(124.63, -128.59) * mm});
            skLineSegment(sketch, "E100.top", {"start": v(62.28, -157.93) * mm, "end": v(124.63, -157.93) * mm});
            skLineSegment(sketch, "E100.left", {"start": v(59.74, -131.13) * mm, "end": v(59.74, -155.39) * mm});
            skLineSegment(sketch, "E100.right", {"start": v(127.17, -131.13) * mm, "end": v(127.17, -155.39) * mm});
            skLineSegment(sketch, "E101", {"start": v(93.45, -157.93) * mm, "end": v(93.45, -128.59) * mm, "construction": true});
            skLineSegment(sketch, "E102", {"start": v(127.17, -143.26) * mm, "end": v(59.74, -143.26) * mm, "construction": true});
            skPoint(sketch, "E103.visualSharp", {"position": v(59.74, -157.93) * mm});
            skArc(sketch, "E103.filletArc", {"start": v(59.74, -155.39) * mm, "mid": v(60.48, -157.18) * mm, "end": v(62.28, -157.93) * mm});
            skPoint(sketch, "E104.visualSharp", {"position": v(127.17, -157.93) * mm});
            skArc(sketch, "E104.filletArc", {"start": v(124.63, -157.93) * mm, "mid": v(126.43, -157.18) * mm, "end": v(127.17, -155.39) * mm});
            skPoint(sketch, "E105.visualSharp", {"position": v(127.17, -128.59) * mm});
            skArc(sketch, "E105.filletArc", {"start": v(127.17, -131.13) * mm, "mid": v(126.43, -129.33) * mm, "end": v(124.63, -128.59) * mm});
            skPoint(sketch, "E106.visualSharp", {"position": v(59.74, -128.59) * mm});
            skArc(sketch, "E106.filletArc", {"start": v(62.28, -128.59) * mm, "mid": v(60.48, -129.33) * mm, "end": v(59.74, -131.13) * mm});
            skLineSegment(sketch, "E107.bottom", {"start": v(62.28, -77.79) * mm, "end": v(124.63, -77.79) * mm});
            skLineSegment(sketch, "E107.top", {"start": v(62.28, -107.13) * mm, "end": v(124.63, -107.13) * mm});
            skLineSegment(sketch, "E107.left", {"start": v(59.74, -80.33) * mm, "end": v(59.74, -104.59) * mm});
            skLineSegment(sketch, "E107.right", {"start": v(127.17, -80.33) * mm, "end": v(127.17, -104.59) * mm});
            skLineSegment(sketch, "E108", {"start": v(93.45, -107.13) * mm, "end": v(93.45, -77.79) * mm, "construction": true});
            skLineSegment(sketch, "E109", {"start": v(127.17, -92.46) * mm, "end": v(59.74, -92.46) * mm, "construction": true});
            skPoint(sketch, "E110.visualSharp", {"position": v(59.74, -107.13) * mm});
            skArc(sketch, "E110.filletArc", {"start": v(59.74, -104.59) * mm, "mid": v(60.48, -106.38) * mm, "end": v(62.28, -107.13) * mm});
            skPoint(sketch, "E111.visualSharp", {"position": v(127.17, -107.13) * mm});
            skArc(sketch, "E111.filletArc", {"start": v(124.63, -107.13) * mm, "mid": v(126.43, -106.38) * mm, "end": v(127.17, -104.59) * mm});
            skPoint(sketch, "E112.visualSharp", {"position": v(127.17, -77.79) * mm});
            skArc(sketch, "E112.filletArc", {"start": v(127.17, -80.33) * mm, "mid": v(126.43, -78.53) * mm, "end": v(124.63, -77.79) * mm});
            skPoint(sketch, "E113.visualSharp", {"position": v(59.74, -77.79) * mm});
            skArc(sketch, "E113.filletArc", {"start": v(62.28, -77.79) * mm, "mid": v(60.48, -78.53) * mm, "end": v(59.74, -80.33) * mm});
            skSolve(sketch);
        }
        {
            var Q0;
            Q0=makeQuery(id+"F14.imprint","IMPRINT",FACE,{"disambiguationData":[TD([[makeQuery(id+"F14.imprint","IMPRINT",EDGE,{"derivedFrom":sQuery(id+"F14.wireOp",EDGE,"E89.left")}),1.0]])]});
            var Q1;
            Q1=makeQuery(id+"F14.imprint","IMPRINT",FACE,{"disambiguationData":[TD([[makeQuery(id+"F14.imprint","IMPRINT",EDGE,{"derivedFrom":sQuery(id+"F14.wireOp",EDGE,"E89.right")}),-1.0]])]});
            var Q2;
            Q2=makeQuery(id+"F14.imprint","IMPRINT",FACE,{"disambiguationData":[TD([[makeQuery(id+"F14.imprint","IMPRINT",EDGE,{"derivedFrom":sQuery(id+"F14.wireOp",EDGE,"E100.left")}),1.0]])]});
            var Q3;
            Q3=makeQuery(id+"F14.imprint","IMPRINT",FACE,{"disambiguationData":[TD([[makeQuery(id+"F14.imprint","IMPRINT",EDGE,{"derivedFrom":sQuery(id+"F14.wireOp",EDGE,"E100.right")}),-1.0]])]});
            var Q4;
            Q4=makeQuery(id+"F14.imprint","IMPRINT",FACE,{"disambiguationData":[TD([[makeQuery(id+"F14.imprint","IMPRINT",EDGE,{"derivedFrom":sQuery(id+"F14.wireOp",EDGE,"E107.right")}),-1.0]])]});
            var Q5;
            Q5=makeQuery(id+"F14.imprint","IMPRINT",FACE,{"disambiguationData":[TD([[makeQuery(id+"F14.imprint","IMPRINT",EDGE,{"derivedFrom":sQuery(id+"F14.wireOp",EDGE,"E107.left")}),1.0]])]});
            extrude(context, id + "F15", {"entities" : qUnion([Q0, Q1, Q2, Q3, Q4, Q5]), "operationType" : NewBodyOperationType.ADD, "depth" : 6.35 * mm});
        }
        {
            var Q0;
            Q0=makeQuery(id+"F15.opExtrude","CAP_EDGE",EDGE,{"disambiguationData":[OSD([sQuery(id+"F14.wireOp",EDGE,"E89.top")])],"isStart":false});
            var Q1;
            Q1=makeQuery(id+"F15.opExtrude","CAP_EDGE",EDGE,{"disambiguationData":[OSD([sQuery(id+"F14.wireOp",EDGE,"E100.top")])],"isStart":false});
            var Q2;
            Q2=makeQuery(id+"F15.opExtrude","CAP_EDGE",EDGE,{"disambiguationData":[OSD([sQuery(id+"F14.wireOp",EDGE,"E107.top")])],"isStart":false});
            fillet(context, id + "F16", {"entities" : qUnion([Q0, Q1, Q2]), "radius" : 2.54 * mm, "tangentPropagation" : true, "allowEdgeOverflow" : false});
        }
        {
            var Q0;
            {var subQ17=sQuery(id+"F14.wireOp",EDGE,"E77.1");Q0=makeQuery(id+"F14.imprint","IMPRINT",FACE,{"disambiguationData":[TD([[makeQuery(id+"F14.imprint","IMPRINT",EDGE,{"derivedFrom":subQ17}),-1.0]])]});}
            var Q1;
            {var subQ23=sQuery(id+"F14.wireOp",EDGE,"E77.4");Q1=makeQuery(id+"F14.imprint","IMPRINT",FACE,{"disambiguationData":[TD([[makeQuery(id+"F14.imprint","IMPRINT",EDGE,{"derivedFrom":subQ23}),-1.0]])]});}
            extrude(context, id + "F17", {"entities" : qUnion([Q0, Q1]), "operationType" : NewBodyOperationType.ADD, "depth" : 2.3 * mm});
        }
        {
            var Q0;
            Q0=makeQuery(id+"F17.opExtrude","CAP_EDGE",EDGE,{"disambiguationData":[OSD([sQuery(id+"F14.wireOp",EDGE,"E81.filletArc")])],"isStart":false});
            chamfer(context, id + "F18", {"entities" : qUnion([Q0]), "width" : 2.3 * mm, "tangentPropagation" : true});
        }
    });
